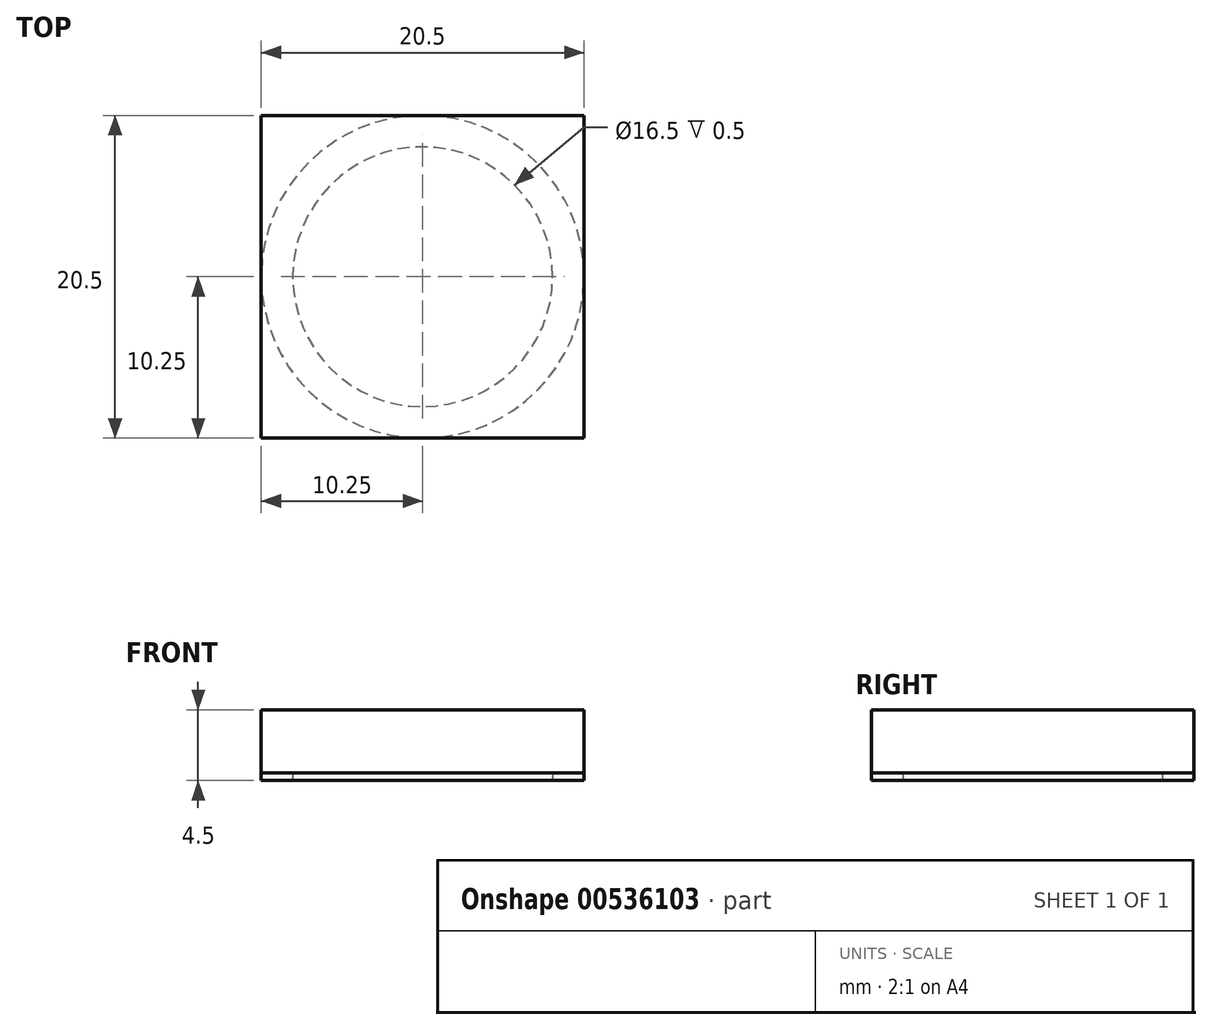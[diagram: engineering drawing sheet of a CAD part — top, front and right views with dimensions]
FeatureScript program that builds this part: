
annotation { "Feature Type Name" : "Feature", "Feature Type Description" : "" }
export const myFeature = defineFeature(function(context is Context, id is Id, definition is map)
    precondition{}
    {
        {
            var Q0;
            Q0=qCreatedBy(makeId("Top.planeOp"),FACE);
            var sketch = newSketch(context, id + "F0", { "sketchPlane" : qUnion([Q0])});
            skCircle(sketch, "E0", {"center": v(0, 0) * mm, "radius": 8.25 * mm});
            skCircle(sketch, "E1", {"center": v(0, 0) * mm, "radius": 10.25 * mm});
            skSolve(sketch);
        }
        {
            var Q0;
            Q0 = qSketchRegion(id + "F0", true);
            extrude(context, id + "F1", {"entities" : qUnion([Q0]), "depth" : 0.5 * mm, "offsetDistance" : 25 * mm});
        }
        {
            var Q0;
            Q0=makeQuery(id+"F1.opExtrude","CAP_FACE",FACE,{"disambiguationData":[OSD([sQuery(id+"F0.wireOp",EDGE,"E0"),sQuery(id+"F0.wireOp",EDGE,"E1")])],"isStart":false});
            var sketch = newSketch(context, id + "F2", { "sketchPlane" : qUnion([Q0])});
            skLineSegment(sketch, "E2.bottom", {"start": v(10.25, 10.25) * mm, "end": v(-10.25, 10.25) * mm});
            skLineSegment(sketch, "E2.top", {"start": v(10.25, -10.25) * mm, "end": v(-10.25, -10.25) * mm});
            skLineSegment(sketch, "E2.left", {"start": v(10.25, 10.25) * mm, "end": v(10.25, -10.25) * mm});
            skLineSegment(sketch, "E2.right", {"start": v(-10.25, 10.25) * mm, "end": v(-10.25, -10.25) * mm});
            skPoint(sketch, "E2.middle", {"position": v(0, 0) * mm});
            skSolve(sketch);
        }
        {
            var Q0;
            Q0 = qSketchRegion(id + "F2", true);
            extrude(context, id + "F3", {"entities" : qUnion([Q0]), "operationType" : NewBodyOperationType.ADD, "depth" : 4 * mm, "offsetDistance" : 25 * mm});
        }
    });
